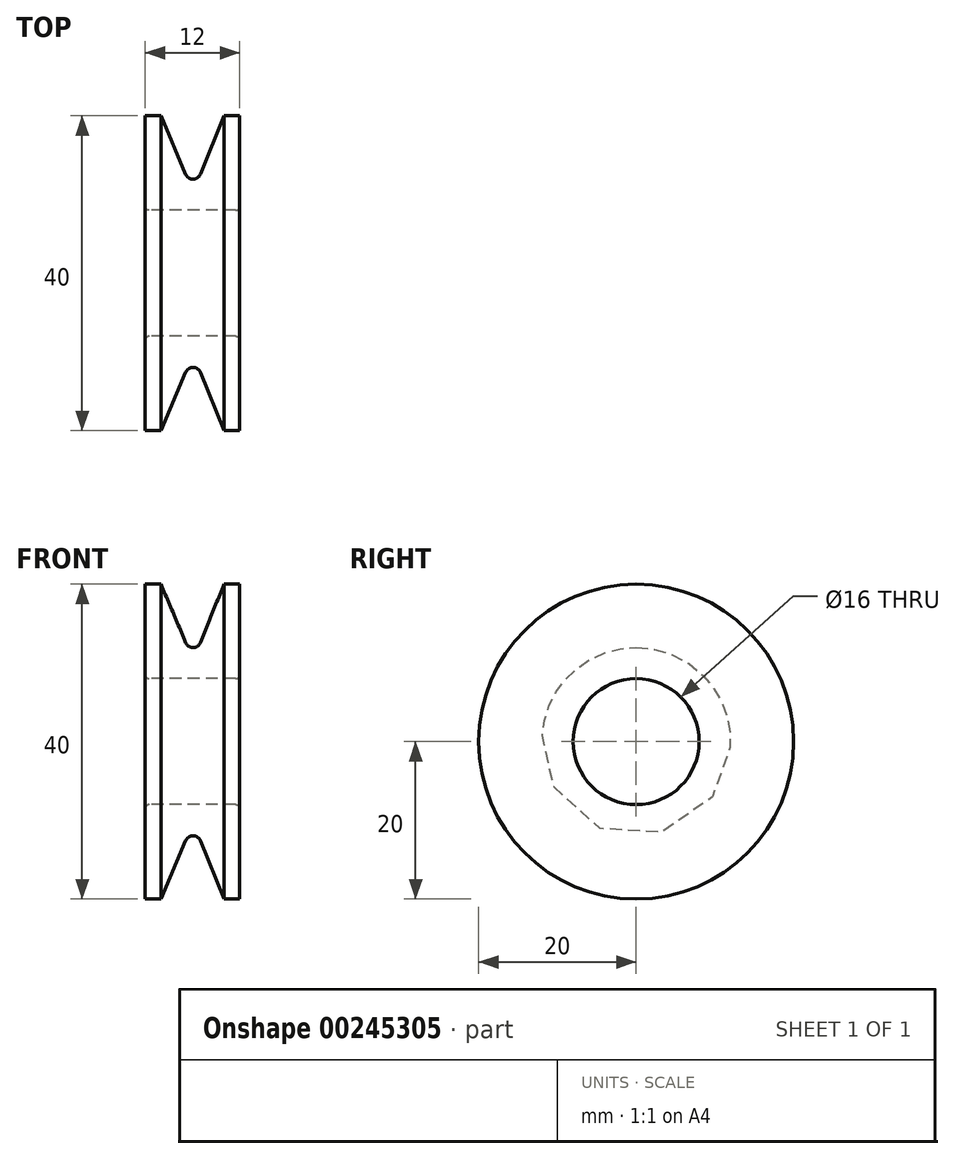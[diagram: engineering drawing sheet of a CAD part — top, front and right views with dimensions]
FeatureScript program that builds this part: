
annotation { "Feature Type Name" : "Feature", "Feature Type Description" : "" }
export const myFeature = defineFeature(function(context is Context, id is Id, definition is map)
    precondition{}
    {
        {
            var Q0;
            Q0=qCreatedBy(makeId("Front.planeOp"),FACE);
            var sketch = newSketch(context, id + "F0", { "sketchPlane" : qUnion([Q0])});
            skLineSegment(sketch, "E0.left", {"start": v(12, 20) * mm, "end": v(12, 8.5) * mm});
            skLineSegment(sketch, "E1", {"start": v(0, 20) * mm, "end": v(0, 8.5) * mm});
            skLineSegment(sketch, "E2", {"start": v(6, 11.97) * mm, "end": v(6, 11.97) * mm});
            skPoint(sketch, "E3.orphan", {"position": v(12, 0) * mm});
            skPoint(sketch, "E4.orphan", {"position": v(0, 0) * mm});
            skLineSegment(sketch, "E5", {"start": v(0, 20) * mm, "end": v(2, 20) * mm});
            skLineSegment(sketch, "E6", {"start": v(2, 20) * mm, "end": v(5.15, 12.57) * mm});
            skLineSegment(sketch, "E7", {"start": v(7, 12.58) * mm, "end": v(10, 20) * mm});
            skLineSegment(sketch, "E8", {"start": v(10, 20) * mm, "end": v(12, 20) * mm});
            skLineSegment(sketch, "E9", {"start": v(6, 0) * mm, "end": v(6, 26.47) * mm, "construction": true});
            skArc(sketch, "E10.filletArc", {"start": v(5.15, 12.57) * mm, "mid": v(6.08, 11.96) * mm, "end": v(7, 12.58) * mm});
            skLineSegment(sketch, "E11", {"start": v(0.5, 8) * mm, "end": v(11.5, 8) * mm});
            skLineSegment(sketch, "E12", {"start": v(0, 0) * mm, "end": v(12, 0) * mm, "construction": true});
            skPoint(sketch, "E13.visualSharp", {"position": v(0, 8) * mm});
            skArc(sketch, "E13.filletArc", {"start": v(0, 8.5) * mm, "mid": v(0.15, 8.15) * mm, "end": v(0.5, 8) * mm});
            skPoint(sketch, "E14.visualSharp", {"position": v(12, 8) * mm});
            skArc(sketch, "E14.filletArc", {"start": v(11.5, 8) * mm, "mid": v(11.85, 8.15) * mm, "end": v(12, 8.5) * mm});
            skSolve(sketch);
        }
        {
            var Q0;
            Q0 = qSketchRegion(id + "F0", true);
            var Q1;
            Q1=sQuery(id+"F0.wireOp",EDGE,"E12");
            revolve(context, id + "F1", {"surfaceOperationType" : NewSurfaceOperationType.NEW, "entities" : qUnion([Q0]), "axis" : qUnion([Q1]), "revolveType" : RevolveType.FULL});
        }
    });
